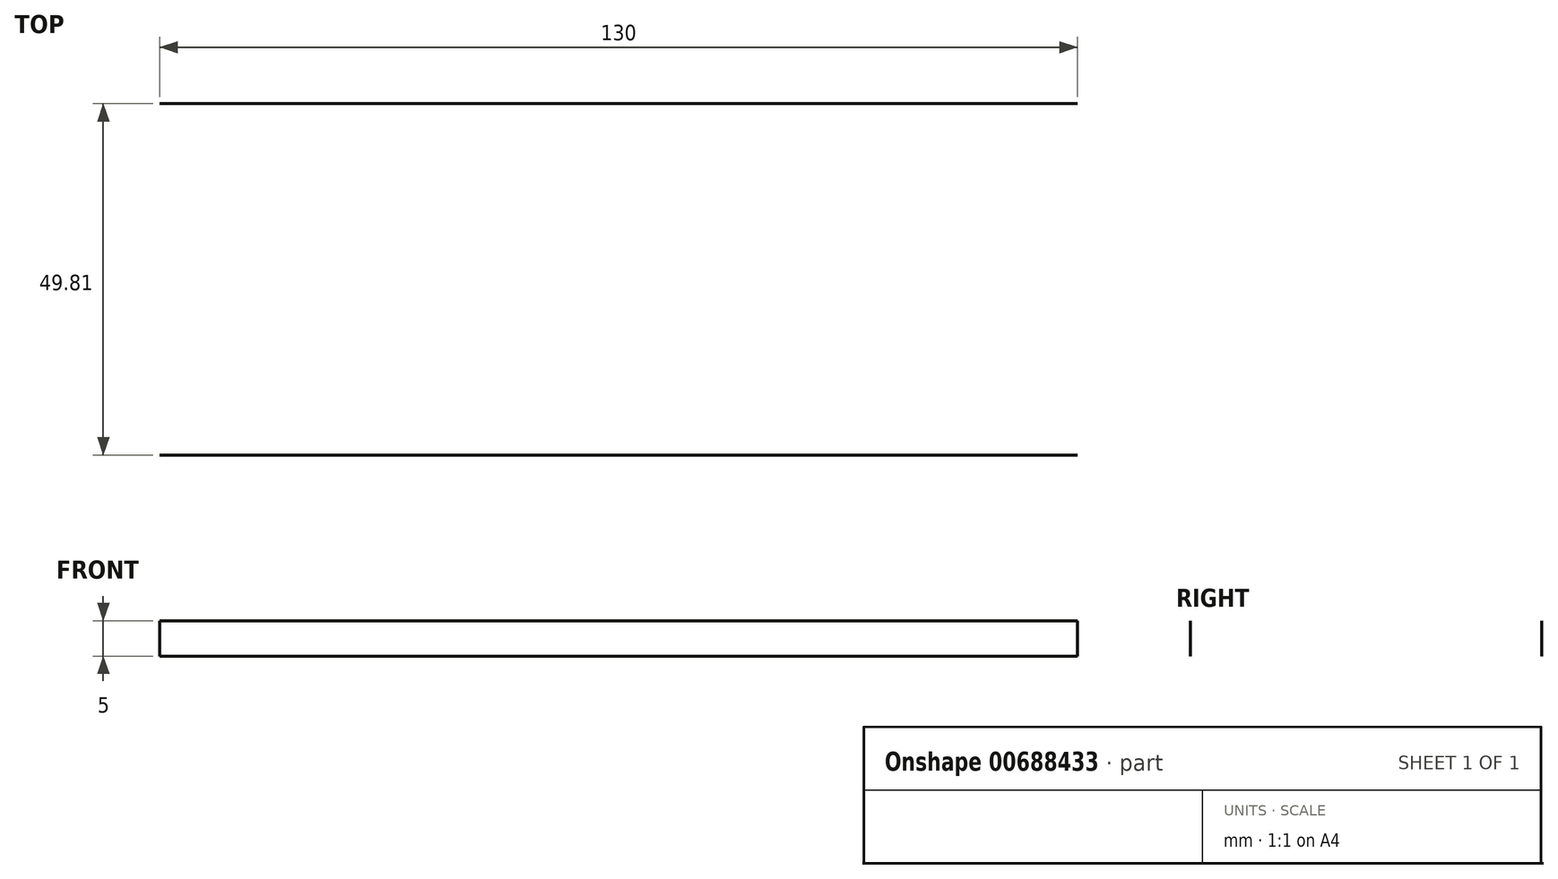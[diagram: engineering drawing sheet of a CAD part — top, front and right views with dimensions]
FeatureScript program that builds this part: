
annotation { "Feature Type Name" : "Feature", "Feature Type Description" : "" }
export const myFeature = defineFeature(function(context is Context, id is Id, definition is map)
    precondition{}
    {
        {
            var Q0;
            Q0=qCreatedBy(makeId("Top.planeOp"),FACE);
            var sketch = newSketch(context, id + "F0", { "sketchPlane" : qUnion([Q0])});
            skLineSegment(sketch, "E0", {"start": v(-62.33, 0) * mm, "end": v(67.67, 0) * mm});
            skSolve(sketch);
        }
        {
            var Q0;
            Q0=sQuery(id+"F0.wireOp",EDGE,"E0");
            extrude(context, id + "F1", {"bodyType" : ToolBodyType.SURFACE, "surfaceEntities" : qUnion([Q0]), "depth" : 5 * mm, "offsetDistance" : 25 * mm});
        }
        {
            var Q0;
            Q0=qCreatedBy(makeId("Top.planeOp"),FACE);
            var sketch = newSketch(context, id + "F2", { "sketchPlane" : qUnion([Q0])});
            skLineSegment(sketch, "E1", {"start": v(-62.33, -49.8) * mm, "end": v(67.67, -49.8) * mm});
            skSolve(sketch);
        }
        {
            var Q0;
            Q0=sQuery(id+"F2.wireOp",EDGE,"E1");
            extrude(context, id + "F3", {"bodyType" : ToolBodyType.SURFACE, "surfaceEntities" : qUnion([Q0]), "depth" : 5 * mm, "offsetDistance" : 25 * mm});
        }
    });
